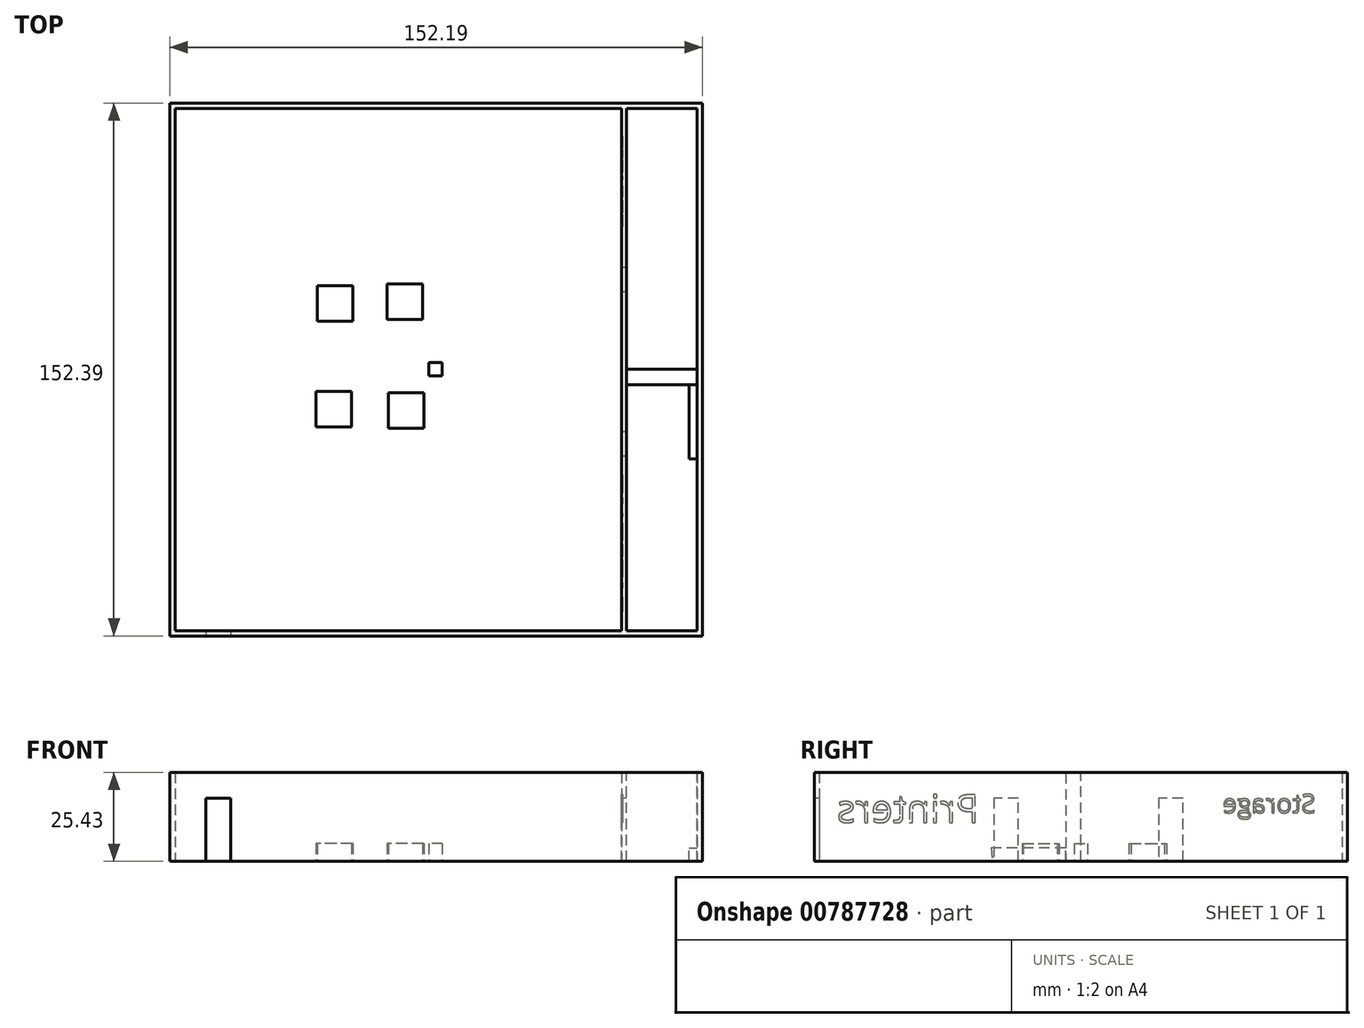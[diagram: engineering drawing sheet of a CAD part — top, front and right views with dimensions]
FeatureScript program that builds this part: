
annotation { "Feature Type Name" : "Feature", "Feature Type Description" : "" }
export const myFeature = defineFeature(function(context is Context, id is Id, definition is map)
    precondition{}
    {
        {
            var Q0;
            Q0=qCreatedBy(makeId("Top.planeOp"),FACE);
            var sketch = newSketch(context, id + "F0", { "sketchPlane" : qUnion([Q0])});
            skLineSegment(sketch, "E0", {"start": v(-75.94, 0) * mm, "end": v(-76.1, 0) * mm});
            skLineSegment(sketch, "E1", {"start": v(76.25, 0) * mm, "end": v(76.29, 0) * mm});
            skLineSegment(sketch, "E2", {"start": v(0, 76.1) * mm, "end": v(-75.94, 76.1) * mm});
            skLineSegment(sketch, "E3", {"start": v(-75.94, 76.1) * mm, "end": v(-75.94, -76.29) * mm});
            skLineSegment(sketch, "E4", {"start": v(-75.94, -76.29) * mm, "end": v(76.25, -76.29) * mm});
            skLineSegment(sketch, "E5", {"start": v(76.25, -76.29) * mm, "end": v(76.25, 76.1) * mm});
            skLineSegment(sketch, "E6", {"start": v(76.25, 76.1) * mm, "end": v(0, 76.1) * mm});
            skSolve(sketch);
        }
        {
            var Q0;
            Q0 = qSketchRegion(id + "F0", true);
            extrude(context, id + "F1", {"entities" : qUnion([Q0]), "depth" : 0.03 * mm, "offsetDistance" : 25.4 * mm});
        }
        {
            var Q0;
            Q0=makeQuery(id+"F1.opExtrude","CAP_FACE",FACE,{"disambiguationData":[OSD([sQuery(id+"F0.wireOp",EDGE,"E2"),sQuery(id+"F0.wireOp",EDGE,"E3"),sQuery(id+"F0.wireOp",EDGE,"E4"),sQuery(id+"F0.wireOp",EDGE,"E5"),sQuery(id+"F0.wireOp",EDGE,"E6")])],"isStart":false});
            var sketch = newSketch(context, id + "F2", { "sketchPlane" : qUnion([Q0])});
            skLineSegment(sketch, "E7", {"start": v(-75.94, 76.1) * mm, "end": v(-75.94, -76.29) * mm});
            skLineSegment(sketch, "E8", {"start": v(-75.94, -76.29) * mm, "end": v(-74.47, -76.29) * mm});
            skLineSegment(sketch, "E9", {"start": v(-74.47, -76.29) * mm, "end": v(-74.47, 76.1) * mm});
            skLineSegment(sketch, "E10", {"start": v(-74.47, 76.1) * mm, "end": v(-75.94, 76.1) * mm});
            skLineSegment(sketch, "E11", {"start": v(-75.94, 76.1) * mm, "end": v(-74.47, 76.1) * mm});
            skLineSegment(sketch, "E12", {"start": v(-74.47, -76.29) * mm, "end": v(76.25, -76.29) * mm});
            skLineSegment(sketch, "E13", {"start": v(76.25, -76.29) * mm, "end": v(76.25, -74.81) * mm});
            skLineSegment(sketch, "E14", {"start": v(76.25, -74.81) * mm, "end": v(-74.47, -74.81) * mm});
            skLineSegment(sketch, "E15", {"start": v(76.25, -76.29) * mm, "end": v(76.25, 76.1) * mm});
            skLineSegment(sketch, "E16", {"start": v(76.25, 76.1) * mm, "end": v(74.78, 76.1) * mm});
            skLineSegment(sketch, "E17", {"start": v(74.78, 76.1) * mm, "end": v(74.78, -76.29) * mm});
            skLineSegment(sketch, "E18", {"start": v(76.25, 76.1) * mm, "end": v(-75.94, 76.1) * mm});
            skLineSegment(sketch, "E19", {"start": v(76.25, 74.62) * mm, "end": v(-75.94, 74.62) * mm});
            skSolve(sketch);
        }
        {
            var Q0;
            Q0 = qSketchRegion(id + "F2", true);
            extrude(context, id + "F3", {"entities" : qUnion([Q0]), "operationType" : NewBodyOperationType.ADD, "depth" : 25.4 * mm, "offsetDistance" : 25.4 * mm});
        }
        {
            var Q0;
            Q0=makeQuery(id+"F3.boolean.opBoolean","MERGE",FACE,{"derivedFrom":[makeQuery(id+"F1.opExtrude","SWEPT_FACE",FACE,{"disambiguationData":[OSD([sQuery(id+"F0.wireOp",EDGE,"E4")])]}),makeQuery(id+"F3.opExtrude","SWEPT_FACE",FACE,{"disambiguationData":[OSD([sQuery(id+"F2.wireOp",EDGE,"E8"),sQuery(id+"F2.wireOp",EDGE,"E12")])]})]});
            var sketch = newSketch(context, id + "F4", { "sketchPlane" : qUnion([Q0])});
            skLineSegment(sketch, "E20", {"start": v(-65.64, 0) * mm, "end": v(-65.64, 18.06) * mm});
            skLineSegment(sketch, "E21", {"start": v(-65.64, 18.06) * mm, "end": v(-58.64, 18.06) * mm});
            skLineSegment(sketch, "E22", {"start": v(-58.64, 18.06) * mm, "end": v(-58.64, 0) * mm});
            skSolve(sketch);
        }
        {
            var Q0;
            Q0 = qSketchRegion(id + "F4", true);
            var Q1;
            {var subQ0=sQuery(id+"F4.wireOp",EDGE,"E20");Q1=makeQuery(id+"F4.imprint","IMPRINT",FACE,{"disambiguationData":[TD([[makeQuery(id+"F4.imprint","IMPRINT",EDGE,{"derivedFrom":subQ0}),-1.0]])]});}
            extrude(context, id + "F5", {"entities" : qUnion([Q0, Q1]), "operationType" : NewBodyOperationType.REMOVE, "oppositeDirection" : true, "depth" : 1.52 * mm, "offsetDistance" : 25.4 * mm});
        }
        {
            var Q0;
            Q0=makeQuery(id+"F1.opExtrude","CAP_FACE",FACE,{"disambiguationData":[OSD([sQuery(id+"F0.wireOp",EDGE,"E2"),sQuery(id+"F0.wireOp",EDGE,"E3"),sQuery(id+"F0.wireOp",EDGE,"E4"),sQuery(id+"F0.wireOp",EDGE,"E5"),sQuery(id+"F0.wireOp",EDGE,"E6")])],"isStart":false});
            var sketch = newSketch(context, id + "F6", { "sketchPlane" : qUnion([Q0])});
            skLineSegment(sketch, "E23.bottom", {"start": v(-3.78, 14.27) * mm, "end": v(-13.94, 14.27) * mm});
            skLineSegment(sketch, "E23.top", {"start": v(-3.78, 24.43) * mm, "end": v(-13.94, 24.43) * mm});
            skLineSegment(sketch, "E23.left", {"start": v(-3.78, 14.27) * mm, "end": v(-3.78, 24.43) * mm});
            skLineSegment(sketch, "E23.right", {"start": v(-13.94, 14.27) * mm, "end": v(-13.94, 24.43) * mm});
            skPoint(sketch, "E23.middle", {"position": v(-8.86, 19.35) * mm});
            skLineSegment(sketch, "E24.bottom", {"start": v(1.9, -1.9) * mm, "end": v(-1.9, -1.9) * mm});
            skLineSegment(sketch, "E24.top", {"start": v(1.9, 1.9) * mm, "end": v(-1.9, 1.9) * mm});
            skLineSegment(sketch, "E24.left", {"start": v(1.9, -1.9) * mm, "end": v(1.9, 1.9) * mm});
            skLineSegment(sketch, "E24.right", {"start": v(-1.9, -1.9) * mm, "end": v(-1.9, 1.9) * mm});
            skPoint(sketch, "E24.middle", {"position": v(0, 0) * mm});
            skLineSegment(sketch, "E25.bottom", {"start": v(-3.4, -16.87) * mm, "end": v(-13.56, -16.87) * mm});
            skLineSegment(sketch, "E25.top", {"start": v(-3.4, -6.71) * mm, "end": v(-13.56, -6.71) * mm});
            skLineSegment(sketch, "E25.left", {"start": v(-3.4, -16.87) * mm, "end": v(-3.4, -6.71) * mm});
            skLineSegment(sketch, "E25.right", {"start": v(-13.56, -16.87) * mm, "end": v(-13.56, -6.71) * mm});
            skPoint(sketch, "E25.middle", {"position": v(-8.48, -11.8) * mm});
            skLineSegment(sketch, "E26.bottom", {"start": v(-23.65, 13.7) * mm, "end": v(-33.8, 13.7) * mm});
            skLineSegment(sketch, "E26.top", {"start": v(-23.65, 23.86) * mm, "end": v(-33.8, 23.86) * mm});
            skLineSegment(sketch, "E26.left", {"start": v(-23.65, 13.7) * mm, "end": v(-23.65, 23.86) * mm});
            skLineSegment(sketch, "E26.right", {"start": v(-33.8, 13.7) * mm, "end": v(-33.8, 23.86) * mm});
            skPoint(sketch, "E26.middle", {"position": v(-28.73, 18.78) * mm});
            skLineSegment(sketch, "E27.bottom", {"start": v(-24.03, -16.5) * mm, "end": v(-34.2, -16.5) * mm});
            skLineSegment(sketch, "E27.top", {"start": v(-24.03, -6.33) * mm, "end": v(-34.2, -6.33) * mm});
            skLineSegment(sketch, "E27.left", {"start": v(-24.03, -16.5) * mm, "end": v(-24.03, -6.33) * mm});
            skLineSegment(sketch, "E27.right", {"start": v(-34.2, -16.5) * mm, "end": v(-34.2, -6.33) * mm});
            skPoint(sketch, "E27.middle", {"position": v(-29.11, -11.41) * mm});
            skLineSegment(sketch, "E28", {"start": v(74.78, 19.02) * mm, "end": v(69.44, 19.02) * mm});
            skLineSegment(sketch, "E29", {"start": v(69.44, 19.02) * mm, "end": v(69.44, 5.24) * mm});
            skLineSegment(sketch, "E30", {"start": v(69.44, 5.24) * mm, "end": v(74.78, 5.24) * mm});
            skSolve(sketch);
        }
        {
            var Q0;
            Q0 = qSketchRegion(id + "F6", true);
            extrude(context, id + "F7", {"entities" : qUnion([Q0]), "operationType" : NewBodyOperationType.ADD, "depth" : 5.08 * mm, "offsetDistance" : 25.4 * mm});
        }
        {
            var Q0;
            Q0=makeQuery(id+"F3.opExtrude","SWEPT_FACE",FACE,{"disambiguationData":[OSD([sQuery(id+"F2.wireOp",EDGE,"E17")])]});
            var sketch = newSketch(context, id + "F8", { "sketchPlane" : qUnion([Q0])});
            skSolve(sketch);
        }
        {
            var Q0;
            Q0=makeQuery(id+"F3.opExtrude","SWEPT_FACE",FACE,{"disambiguationData":[OSD([sQuery(id+"F2.wireOp",EDGE,"E14")])]});
            var sketch = newSketch(context, id + "F9", { "sketchPlane" : qUnion([Q0])});
            skLineSegment(sketch, "E31", {"start": v(-74.78, 0.03) * mm, "end": v(-54.6, 0.03) * mm});
            skLineSegment(sketch, "E32", {"start": v(-54.6, 0.03) * mm, "end": v(-54.6, 25.43) * mm});
            skLineSegment(sketch, "E33", {"start": v(-54.6, 25.43) * mm, "end": v(-53.13, 25.43) * mm});
            skLineSegment(sketch, "E34", {"start": v(-53.13, 25.43) * mm, "end": v(-53.13, 0) * mm});
            skLineSegment(sketch, "E35", {"start": v(-53.13, 0) * mm, "end": v(-54.6, 0.03) * mm});
            skSolve(sketch);
        }
        {
            var Q0;
            Q0 = qSketchRegion(id + "F9", true);
            extrude(context, id + "F10", {"entities" : qUnion([Q0]), "operationType" : NewBodyOperationType.ADD, "depth" : 149.86 * mm, "offsetDistance" : 25.4 * mm});
        }
        {
            var Q0;
            Q0 = qSketchRegion(id + "F9", true);
            extrude(context, id + "F11", {"entities" : qUnion([Q0]), "operationType" : NewBodyOperationType.ADD, "oppositeDirection" : true, "depth" : 0.5 * mm, "offsetDistance" : 25.4 * mm});
        }
        {
            var Q0;
            Q0=makeQuery(id+"F10.opExtrude","SWEPT_FACE",FACE,{"disambiguationData":[OSD([sQuery(id+"F9.wireOp",EDGE,"E34")])]});
            var sketch = newSketch(context, id + "F12", { "sketchPlane" : qUnion([Q0])});
            skLineSegment(sketch, "E36", {"start": v(17.92, 0.03) * mm, "end": v(17.92, 18.08) * mm});
            skLineSegment(sketch, "E37", {"start": v(17.92, 18.08) * mm, "end": v(24.93, 18.08) * mm});
            skLineSegment(sketch, "E38", {"start": v(24.93, 18.08) * mm, "end": v(24.93, 0) * mm});
            skLineSegment(sketch, "E39", {"start": v(-29.13, 0.03) * mm, "end": v(-29.13, 18.08) * mm});
            skLineSegment(sketch, "E40", {"start": v(-29.13, 18.08) * mm, "end": v(-22.12, 18.08) * mm});
            skLineSegment(sketch, "E41", {"start": v(-22.12, 18.08) * mm, "end": v(-22.12, 0) * mm});
            skSolve(sketch);
        }
        {
            var Q0;
            Q0 = qSketchRegion(id + "F12", true);
            var Q1;
            {var subQ0=sQuery(id+"F12.wireOp",EDGE,"E36");Q1=makeQuery(id+"F12.imprint","IMPRINT",FACE,{"disambiguationData":[TD([[makeQuery(id+"F12.imprint","IMPRINT",EDGE,{"derivedFrom":subQ0}),-1.0]])]});}
            var Q2;
            {var subQ0=sQuery(id+"F12.wireOp",EDGE,"E39");Q2=makeQuery(id+"F12.imprint","IMPRINT",FACE,{"disambiguationData":[TD([[makeQuery(id+"F12.imprint","IMPRINT",EDGE,{"derivedFrom":subQ0}),-1.0]])]});}
            extrude(context, id + "F13", {"entities" : qUnion([Q0, Q1, Q2]), "operationType" : NewBodyOperationType.REMOVE, "oppositeDirection" : true, "depth" : 12.7 * mm, "offsetDistance" : 25.4 * mm});
        }
        {
            var Q0;
            {var subQ0=sQuery(id+"F2.wireOp",EDGE,"E17");Q0=makeQuery(id+"F8.imprint","IMPRINT",FACE,{"disambiguationData":[TD([[makeQuery(id+"F8.imprint","IMPRINT",EDGE,{"derivedFrom":makeQuery(id+"F3.opExtrude","CAP_EDGE",EDGE,{"disambiguationData":[OSD([subQ0])],"isStart":false})}),-1.0]])]});}
            var sketch = newSketch(context, id + "F14", { "sketchPlane" : qUnion([Q0])});
            skLineSegment(sketch, "E42", {"start": v(0, 0) * mm, "end": v(0, 25.24) * mm});
            skLineSegment(sketch, "E43", {"start": v(0, 25.24) * mm, "end": v(4.42, 25.24) * mm});
            skLineSegment(sketch, "E44", {"start": v(4.42, 25.24) * mm, "end": v(4.42, 0) * mm});
            skLineSegment(sketch, "E45", {"start": v(0, 0) * mm, "end": v(4.42, 0) * mm});
            skSolve(sketch);
        }
        {
            var Q0;
            Q0 = qSketchRegion(id + "F14", true);
            extrude(context, id + "F15", {"entities" : qUnion([Q0]), "operationType" : NewBodyOperationType.ADD, "depth" : 20.52 * mm, "offsetDistance" : 25.4 * mm});
        }
        {
            var Q0;
            {var subQ0=sQuery(id+"F2.wireOp",EDGE,"E17");Q0=makeQuery(id+"F8.imprint","IMPRINT",FACE,{"disambiguationData":[TD([[makeQuery(id+"F8.imprint","IMPRINT",EDGE,{"derivedFrom":makeQuery(id+"F3.opExtrude","CAP_EDGE",EDGE,{"disambiguationData":[OSD([subQ0])],"isStart":false})}),-1.0]])]});}
            var sketch = newSketch(context, id + "F16", { "sketchPlane" : qUnion([Q0])});
            skLineSegment(sketch, "E46", {"start": v(4.43, 0) * mm, "end": v(4.43, 3.85) * mm});
            skLineSegment(sketch, "E47", {"start": v(4.43, 3.85) * mm, "end": v(25.67, 3.85) * mm});
            skLineSegment(sketch, "E48", {"start": v(25.67, 3.85) * mm, "end": v(25.34, 0) * mm});
            skLineSegment(sketch, "E49", {"start": v(25.34, 0) * mm, "end": v(4.43, 0) * mm});
            skSolve(sketch);
        }
        {
            var Q0;
            Q0 = qSketchRegion(id + "F16", true);
            extrude(context, id + "F17", {"entities" : qUnion([Q0]), "operationType" : NewBodyOperationType.ADD, "depth" : 2.31 * mm, "offsetDistance" : 25.4 * mm});
        }
        {
            var Q0;
            Q0=makeQuery(id+"F10.opExtrude","SWEPT_FACE",FACE,{"disambiguationData":[OSD([sQuery(id+"F9.wireOp",EDGE,"E34")])]});
            var sketch = newSketch(context, id + "F18", { "sketchPlane" : qUnion([Q0])});
            skText(sketch, "E50", { "text": "Printers\n", "fontName": "OpenSans-Regular.ttf"});
            const initialGuessF18  = {"E50": [0.02913, 0.01113, 1, 0, 0.00797]};
            skSetInitialGuess(sketch, initialGuessF18);
            skSolve(sketch);
        }
        {
            var Q0;
            Q0 = qSketchRegion(id + "F18", true);
            extrude(context, id + "F19", {"entities" : qUnion([Q0]), "operationType" : NewBodyOperationType.REMOVE, "oppositeDirection" : true, "depth" : 0.25 * mm, "offsetDistance" : 25.4 * mm});
        }
        {
            var Q0;
            {var subQ1=sQuery(id+"F2.wireOp",EDGE,"E14");var subQ9=sQuery(id+"F9.wireOp",EDGE,"E34");var subQ10=makeQuery(id+"F10.opExtrude","SWEPT_FACE",FACE,{"disambiguationData":[OSD([subQ9])]});Q0=makeQuery(id+"F19.boolean.opBoolean","SPLIT",FACE,{"disambiguationData":[TD([makeQuery(id+"F3.opExtrude","SWEPT_FACE",FACE,{"disambiguationData":[OSD([subQ1])]})])],"derivedFrom":subQ10});}
            var sketch = newSketch(context, id + "F20", { "sketchPlane" : qUnion([Q0])});
            skText(sketch, "E51", { "text": "Storage\n", "fontName": "OpenSans-Regular.ttf"});
            const initialGuessF20  = {"E51": [-0.06703, 0.01387, 1, 0, 0.00535]};
            skSetInitialGuess(sketch, initialGuessF20);
            skSolve(sketch);
        }
        {
            var Q0;
            Q0 = qSketchRegion(id + "F20", true);
            extrude(context, id + "F21", {"entities" : qUnion([Q0]), "operationType" : NewBodyOperationType.REMOVE, "oppositeDirection" : true, "depth" : 0.25 * mm, "offsetDistance" : 25.4 * mm});
        }
    });
